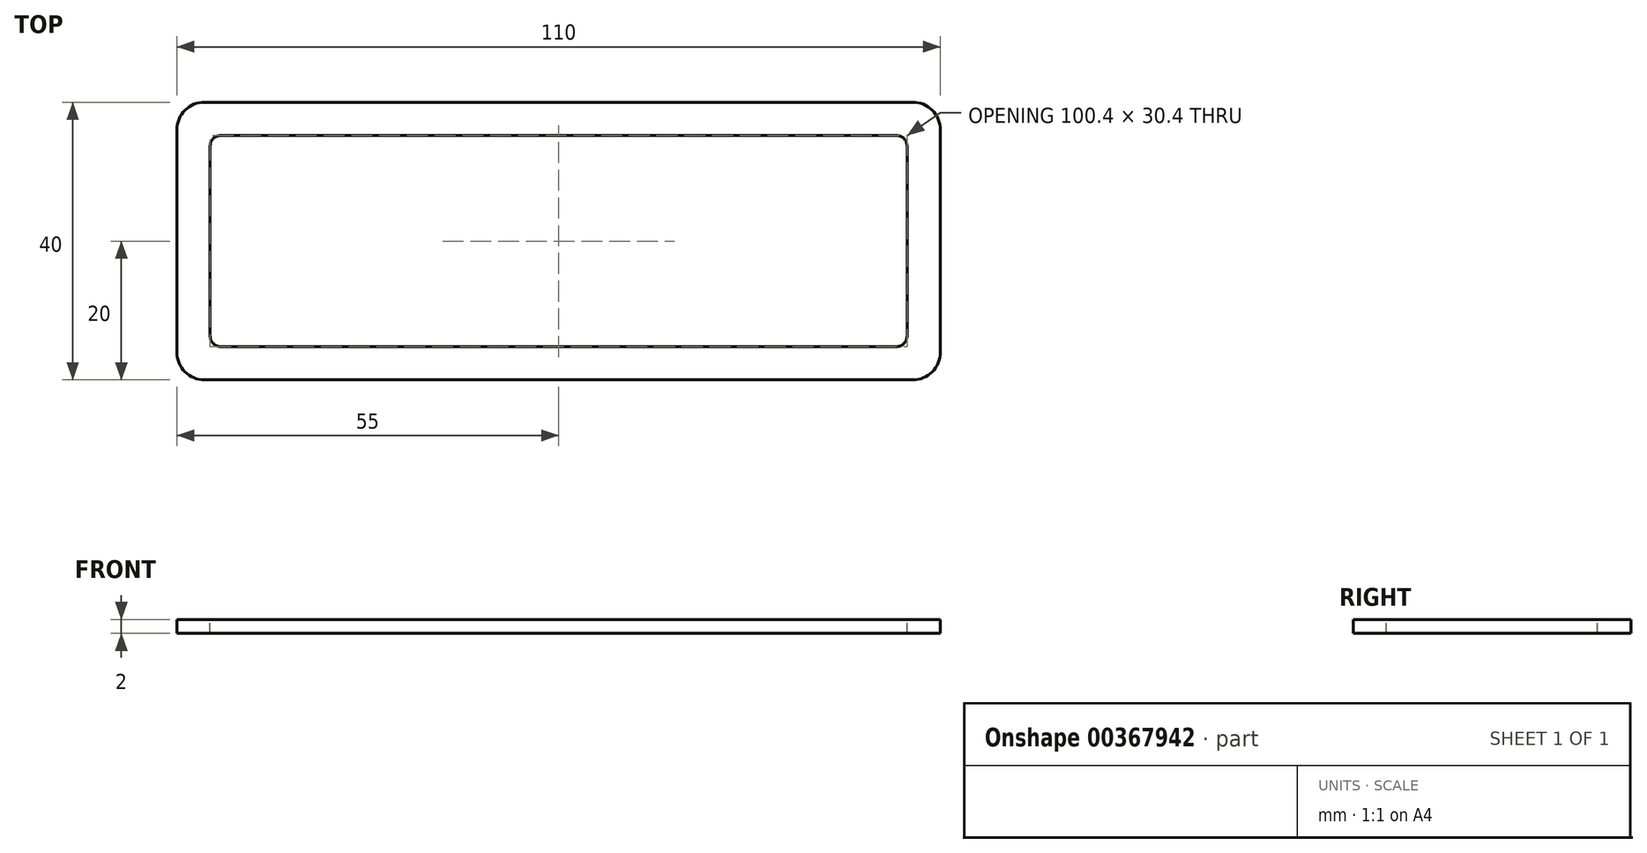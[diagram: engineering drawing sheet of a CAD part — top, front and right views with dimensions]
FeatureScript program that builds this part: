
annotation { "Feature Type Name" : "Feature", "Feature Type Description" : "" }
export const myFeature = defineFeature(function(context is Context, id is Id, definition is map)
    precondition{}
    {
        {
            var Q0;
            Q0=qCreatedBy(makeId("Top.planeOp"),FACE);
            var sketch = newSketch(context, id + "F0", { "sketchPlane" : qUnion([Q0])});
            skLineSegment(sketch, "E0.bottom", {"start": v(55, 20) * mm, "end": v(-55, 20) * mm});
            skLineSegment(sketch, "E0.top", {"start": v(55, -20) * mm, "end": v(-55, -20) * mm});
            skLineSegment(sketch, "E0.left", {"start": v(55, 20) * mm, "end": v(55, -20) * mm});
            skLineSegment(sketch, "E0.right", {"start": v(-55, 20) * mm, "end": v(-55, -20) * mm});
            skPoint(sketch, "E0.middle", {"position": v(0, 0) * mm});
            skSolve(sketch);
        }
        {
            var Q0;
            Q0=makeQuery(id+"F0.imprint","IMPRINT",FACE,{"disambiguationData":[TD([[makeQuery(id+"F0.imprint","IMPRINT",EDGE,{"derivedFrom":sQuery(id+"F0.wireOp",EDGE,"E0.bottom")}),1.0]])]});
            extrude(context, id + "F1", {"entities" : qUnion([Q0]), "depth" : 2 * mm});
        }
        {
            var Q0;
            Q0=makeQuery(id+"F1.opExtrude","CAP_FACE",FACE,{"disambiguationData":[OSD([sQuery(id+"F0.wireOp",EDGE,"E0.bottom"),sQuery(id+"F0.wireOp",EDGE,"E0.top"),sQuery(id+"F0.wireOp",EDGE,"E0.left"),sQuery(id+"F0.wireOp",EDGE,"E0.right")])],"isStart":false});
            var sketch = newSketch(context, id + "F2", { "sketchPlane" : qUnion([Q0])});
            skLineSegment(sketch, "E1.bottom", {"start": v(50.2, 15.2) * mm, "end": v(-50.2, 15.2) * mm});
            skLineSegment(sketch, "E1.top", {"start": v(50.2, -15.2) * mm, "end": v(-50.2, -15.2) * mm});
            skLineSegment(sketch, "E1.left", {"start": v(50.2, 15.2) * mm, "end": v(50.2, -15.2) * mm});
            skLineSegment(sketch, "E1.right", {"start": v(-50.2, 15.2) * mm, "end": v(-50.2, -15.2) * mm});
            skPoint(sketch, "E1.middle", {"position": v(0, 0) * mm});
            skSolve(sketch);
        }
        {
            var Q0;
            Q0=makeQuery(id+"F2.imprint","IMPRINT",FACE,{"disambiguationData":[TD([[makeQuery(id+"F2.imprint","IMPRINT",EDGE,{"derivedFrom":sQuery(id+"F2.wireOp",EDGE,"E1.bottom")}),1.0]])]});
            extrude(context, id + "F3", {"entities" : qUnion([Q0]), "operationType" : NewBodyOperationType.REMOVE, "endBound" : BoundingType.THROUGH_ALL, "oppositeDirection" : true, "depth" : 25 * mm});
        }
        {
            var Q0;
            Q0=makeQuery(id+"F1.opExtrude","SWEPT_EDGE",EDGE,{"disambiguationData":[OSD([sQuery(id+"F0.wireOp",EDGE,"E0.top"),sQuery(id+"F0.wireOp",EDGE,"E0.right")])]});
            var Q1;
            Q1=makeQuery(id+"F1.opExtrude","SWEPT_EDGE",EDGE,{"disambiguationData":[OSD([sQuery(id+"F0.wireOp",EDGE,"E0.bottom"),sQuery(id+"F0.wireOp",EDGE,"E0.right")])]});
            var Q2;
            Q2=makeQuery(id+"F1.opExtrude","SWEPT_EDGE",EDGE,{"disambiguationData":[OSD([sQuery(id+"F0.wireOp",EDGE,"E0.top"),sQuery(id+"F0.wireOp",EDGE,"E0.left")])]});
            var Q3;
            Q3=makeQuery(id+"F1.opExtrude","SWEPT_EDGE",EDGE,{"disambiguationData":[OSD([sQuery(id+"F0.wireOp",EDGE,"E0.bottom"),sQuery(id+"F0.wireOp",EDGE,"E0.left")])]});
            fillet(context, id + "F4", {"entities" : qUnion([Q0, Q1, Q2, Q3]), "radius" : 4 * mm, "tangentPropagation" : true, "allowEdgeOverflow" : false});
        }
        {
            var Q0;
            Q0=makeQuery(id+"F3.boolean.opBoolean","COPY",EDGE,{"derivedFrom":makeQuery(id+"F3.opExtrude","SWEPT_EDGE",EDGE,{"disambiguationData":[OSD([sQuery(id+"F2.wireOp",EDGE,"E1.bottom"),sQuery(id+"F2.wireOp",EDGE,"E1.right")])]})});
            var Q1;
            Q1=makeQuery(id+"F3.boolean.opBoolean","COPY",EDGE,{"derivedFrom":makeQuery(id+"F3.opExtrude","SWEPT_EDGE",EDGE,{"disambiguationData":[OSD([sQuery(id+"F2.wireOp",EDGE,"E1.bottom"),sQuery(id+"F2.wireOp",EDGE,"E1.left")])]})});
            var Q2;
            Q2=makeQuery(id+"F3.boolean.opBoolean","COPY",EDGE,{"derivedFrom":makeQuery(id+"F3.opExtrude","SWEPT_EDGE",EDGE,{"disambiguationData":[OSD([sQuery(id+"F2.wireOp",EDGE,"E1.top"),sQuery(id+"F2.wireOp",EDGE,"E1.right")])]})});
            var Q3;
            Q3=makeQuery(id+"F3.boolean.opBoolean","COPY",EDGE,{"derivedFrom":makeQuery(id+"F3.opExtrude","SWEPT_EDGE",EDGE,{"disambiguationData":[OSD([sQuery(id+"F2.wireOp",EDGE,"E1.top"),sQuery(id+"F2.wireOp",EDGE,"E1.left")])]})});
            fillet(context, id + "F5", {"entities" : qUnion([Q0, Q1, Q2, Q3]), "radius" : 1.5 * mm, "tangentPropagation" : true, "allowEdgeOverflow" : false});
        }
    });
